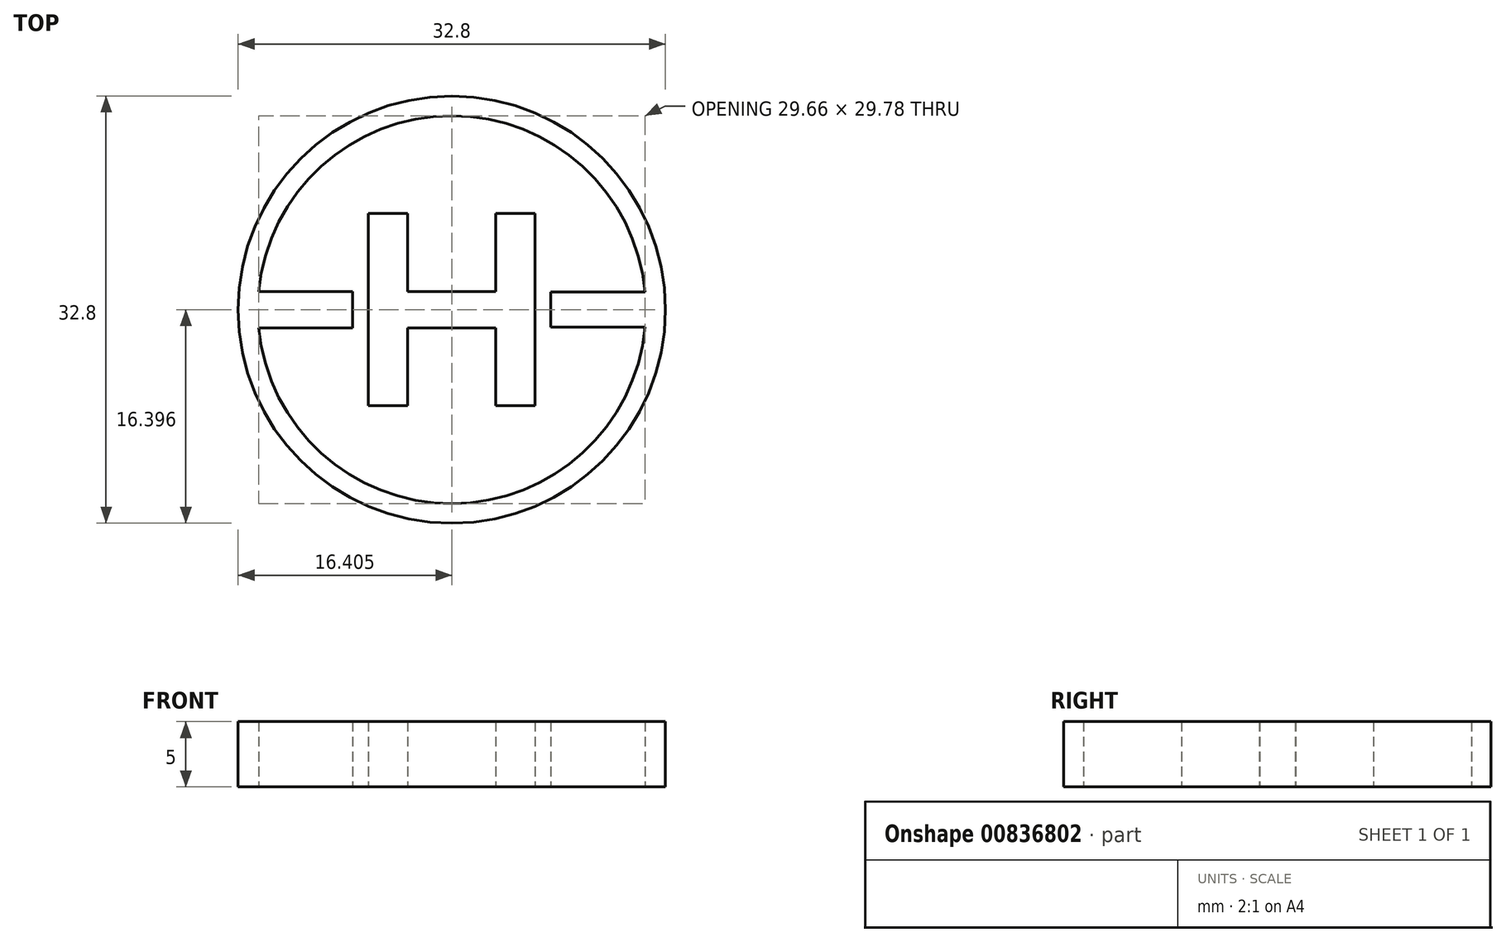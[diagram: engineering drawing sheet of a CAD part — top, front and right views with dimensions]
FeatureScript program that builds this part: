
annotation { "Feature Type Name" : "Feature", "Feature Type Description" : "" }
export const myFeature = defineFeature(function(context is Context, id is Id, definition is map)
    precondition{}
    {
        {
            var Q0;
            Q0=qCreatedBy(makeId("Top.planeOp"),FACE);
            var sketch = newSketch(context, id + "F0", { "sketchPlane" : qUnion([Q0])});
            skCircle(sketch, "E0", {"center": v(0.16, -0.21) * mm, "radius": 16.4 * mm});
            skCircle(sketch, "E1", {"center": v(0.16, -0.21) * mm, "radius": 14.9 * mm});
            skLineSegment(sketch, "E2", {"start": v(15, -1.56) * mm, "end": v(7.76, -1.56) * mm});
            skLineSegment(sketch, "E3", {"start": v(7.76, -1.56) * mm, "end": v(7.76, 1.15) * mm});
            skLineSegment(sketch, "E4", {"start": v(7.76, 1.15) * mm, "end": v(15, 1.15) * mm});
            skLineSegment(sketch, "E5", {"start": v(-14.66, -1.6) * mm, "end": v(-7.45, -1.6) * mm});
            skLineSegment(sketch, "E6", {"start": v(-7.45, -1.6) * mm, "end": v(-7.45, 1.18) * mm});
            skLineSegment(sketch, "E7", {"start": v(-7.45, 1.18) * mm, "end": v(-14.66, 1.18) * mm});
            skLineSegment(sketch, "E8", {"start": v(-3.22, -1.6) * mm, "end": v(-3.22, -7.57) * mm});
            skLineSegment(sketch, "E9", {"start": v(-3.22, -7.57) * mm, "end": v(-6.23, -7.57) * mm});
            skLineSegment(sketch, "E10", {"start": v(-6.23, -7.57) * mm, "end": v(-6.23, 7.17) * mm});
            skLineSegment(sketch, "E11", {"start": v(-6.23, 7.17) * mm, "end": v(-3.22, 7.17) * mm});
            skLineSegment(sketch, "E12", {"start": v(-3.22, 7.17) * mm, "end": v(-3.22, 1.18) * mm});
            skLineSegment(sketch, "E13", {"start": v(-3.22, 1.18) * mm, "end": v(3.54, 1.18) * mm});
            skLineSegment(sketch, "E14", {"start": v(3.54, 1.18) * mm, "end": v(3.54, 7.17) * mm});
            skLineSegment(sketch, "E15", {"start": v(3.54, 7.17) * mm, "end": v(6.55, 7.17) * mm});
            skLineSegment(sketch, "E16", {"start": v(6.55, 7.17) * mm, "end": v(6.55, -7.59) * mm});
            skLineSegment(sketch, "E17", {"start": v(6.55, -7.59) * mm, "end": v(3.54, -7.59) * mm});
            skLineSegment(sketch, "E18", {"start": v(3.54, -7.59) * mm, "end": v(3.54, -1.6) * mm});
            skLineSegment(sketch, "E19", {"start": v(3.54, -1.6) * mm, "end": v(-3.22, -1.6) * mm});
            skPoint(sketch, "E20", {"position": v(-3.22, 4.18) * mm});
            skSolve(sketch);
        }
        {
            var Q0;
            Q0 = qSketchRegion(id + "F0", true);
            var Q1;
            Q1=makeQuery(id+"F0.imprint","IMPRINT",FACE,{"disambiguationData":[TD([[makeQuery(id+"F0.imprint","IMPRINT",EDGE,{"derivedFrom":sQuery(id+"F0.wireOp",EDGE,"E8")}),-1.0]])]});
            var Q2;
            {var subQ0=sQuery(id+"F0.wireOp",EDGE,"E2");Q2=makeQuery(id+"F0.imprint","IMPRINT",FACE,{"disambiguationData":[TD([[makeQuery(id+"F0.imprint","IMPRINT",EDGE,{"derivedFrom":subQ0}),-1.0]])]});}
            var Q3;
            {var subQ0=sQuery(id+"F0.wireOp",EDGE,"E5");Q3=makeQuery(id+"F0.imprint","IMPRINT",FACE,{"disambiguationData":[TD([[makeQuery(id+"F0.imprint","IMPRINT",EDGE,{"derivedFrom":subQ0}),1.0]])]});}
            extrude(context, id + "F1", {"entities" : qUnion([Q0, Q1, Q2, Q3]), "depth" : 5 * mm, "offsetDistance" : 25 * mm});
        }
    });
